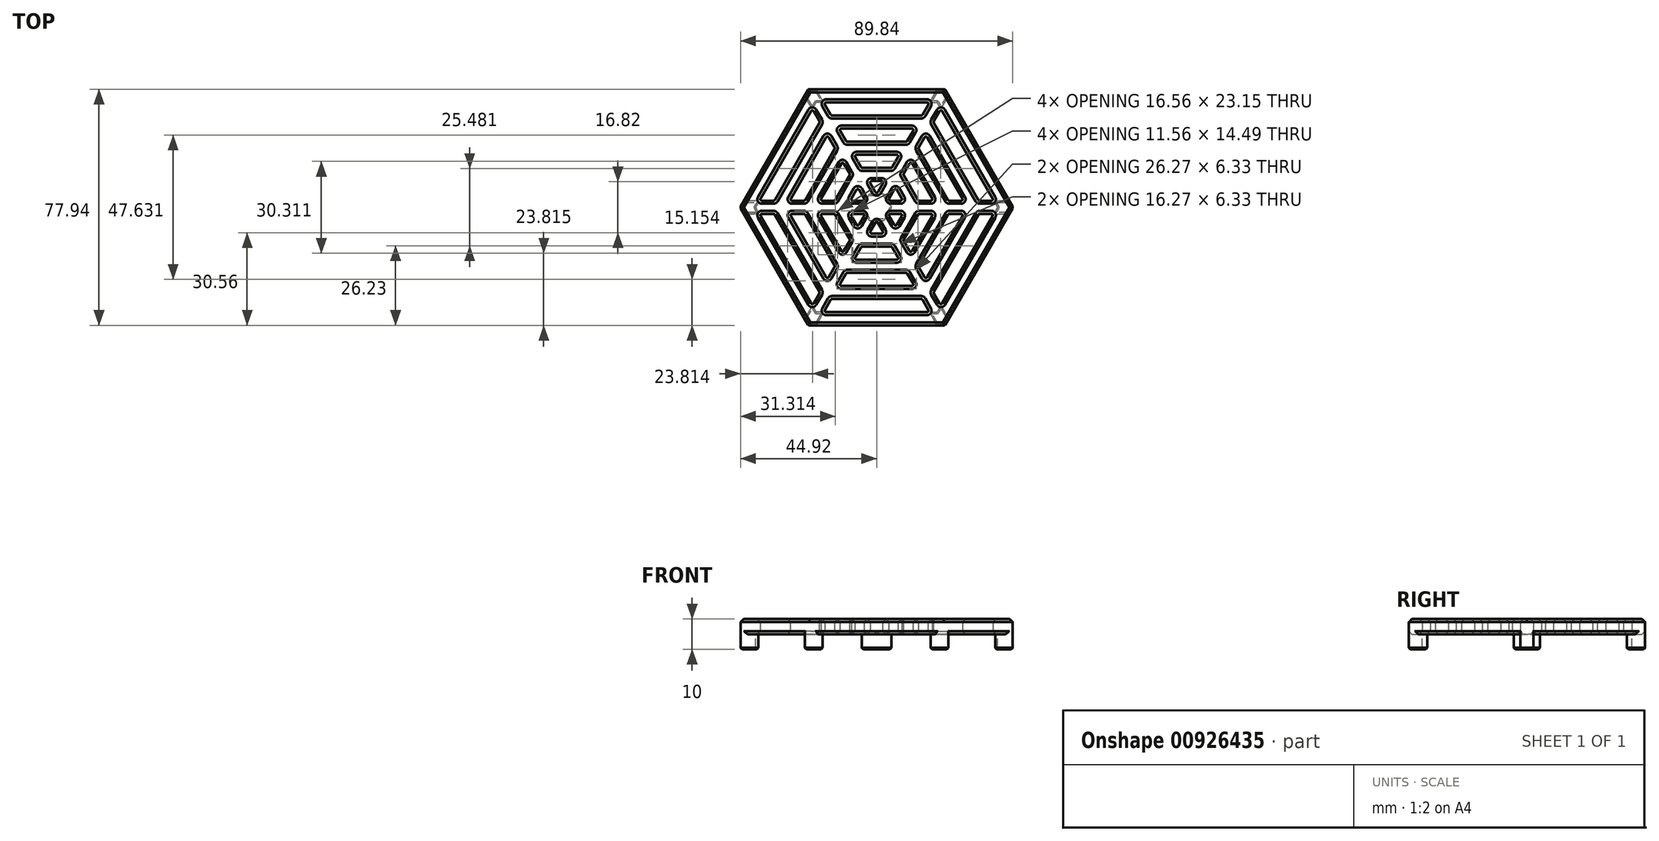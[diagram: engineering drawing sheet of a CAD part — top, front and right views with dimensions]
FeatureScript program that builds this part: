
annotation { "Feature Type Name" : "Feature", "Feature Type Description" : "" }
export const myFeature = defineFeature(function(context is Context, id is Id, definition is map)
    precondition{}
    {
        {
            var Q0;
            Q0=qCreatedBy(makeId("Top.planeOp"),FACE);
            var sketch = newSketch(context, id + "F0", { "sketchPlane" : qUnion([Q0])});
            skCircle(sketch, "E0.cCircle", {"center": v(0, 0) * mm, "radius": 45 * mm, "construction": true});
            skLineSegment(sketch, "E0.0", {"start": v(45, 0) * mm, "end": v(22.5, -38.97) * mm});
            skLineSegment(sketch, "E0.1", {"start": v(22.5, -38.97) * mm, "end": v(-22.5, -38.97) * mm});
            skLineSegment(sketch, "E0.2", {"start": v(-22.5, -38.97) * mm, "end": v(-45, 0) * mm});
            skLineSegment(sketch, "E0.3", {"start": v(-45, 0) * mm, "end": v(-22.5, 38.97) * mm});
            skLineSegment(sketch, "E0.4", {"start": v(-22.5, 38.97) * mm, "end": v(22.5, 38.97) * mm});
            skLineSegment(sketch, "E0.5", {"start": v(22.5, 38.97) * mm, "end": v(45, 0) * mm});
            skCircle(sketch, "E1.cCircle", {"center": v(0, 0) * mm, "radius": 5 * mm, "construction": true});
            skCircle(sketch, "E2.cCircle", {"center": v(0, 0) * mm, "radius": 10 * mm, "construction": true});
            skLineSegment(sketch, "E2.0", {"start": v(8.75, -2.17) * mm, "end": v(6.25, -6.5) * mm});
            skLineSegment(sketch, "E2.1", {"start": v(2.5, -8.66) * mm, "end": v(-2.5, -8.66) * mm});
            skLineSegment(sketch, "E2.2", {"start": v(-6.25, -6.5) * mm, "end": v(-8.75, -2.17) * mm});
            skLineSegment(sketch, "E2.3", {"start": v(-8.75, 2.17) * mm, "end": v(-6.25, 6.5) * mm});
            skLineSegment(sketch, "E2.4", {"start": v(-2.5, 8.66) * mm, "end": v(2.5, 8.66) * mm});
            skLineSegment(sketch, "E2.5", {"start": v(6.25, 6.5) * mm, "end": v(8.75, 2.17) * mm});
            skCircle(sketch, "E3.cCircle", {"center": v(0, 0) * mm, "radius": 15 * mm, "construction": true});
            skLineSegment(sketch, "E3.0", {"start": v(13.75, -2.17) * mm, "end": v(8.75, -10.83) * mm});
            skLineSegment(sketch, "E3.1", {"start": v(5, -13) * mm, "end": v(-5, -13) * mm});
            skLineSegment(sketch, "E3.2", {"start": v(-8.75, -10.83) * mm, "end": v(-13.75, -2.17) * mm});
            skLineSegment(sketch, "E3.3", {"start": v(-13.75, 2.17) * mm, "end": v(-8.75, 10.83) * mm});
            skLineSegment(sketch, "E3.4", {"start": v(-5, 13) * mm, "end": v(5, 13) * mm});
            skLineSegment(sketch, "E3.5", {"start": v(8.75, 10.83) * mm, "end": v(13.75, 2.17) * mm});
            skCircle(sketch, "E4.cCircle", {"center": v(0, 0) * mm, "radius": 20 * mm, "construction": true});
            skLineSegment(sketch, "E4.0", {"start": v(18.75, -2.17) * mm, "end": v(11.25, -15.16) * mm});
            skLineSegment(sketch, "E4.1", {"start": v(7.5, -17.32) * mm, "end": v(-7.5, -17.32) * mm});
            skLineSegment(sketch, "E4.2", {"start": v(-11.25, -15.16) * mm, "end": v(-18.75, -2.17) * mm});
            skLineSegment(sketch, "E4.3", {"start": v(-18.75, 2.17) * mm, "end": v(-11.25, 15.16) * mm});
            skLineSegment(sketch, "E4.4", {"start": v(-7.5, 17.32) * mm, "end": v(7.5, 17.32) * mm});
            skLineSegment(sketch, "E4.5", {"start": v(11.25, 15.16) * mm, "end": v(18.75, 2.17) * mm});
            skCircle(sketch, "E5.cCircle", {"center": v(0, 0) * mm, "radius": 25 * mm, "construction": true});
            skLineSegment(sketch, "E5.0", {"start": v(23.75, -2.17) * mm, "end": v(13.75, -19.49) * mm});
            skLineSegment(sketch, "E5.1", {"start": v(10, -21.65) * mm, "end": v(-10, -21.65) * mm});
            skLineSegment(sketch, "E5.2", {"start": v(-13.75, -19.49) * mm, "end": v(-23.75, -2.17) * mm});
            skLineSegment(sketch, "E5.3", {"start": v(-23.75, 2.17) * mm, "end": v(-13.75, 19.49) * mm});
            skLineSegment(sketch, "E5.4", {"start": v(-10, 21.65) * mm, "end": v(10, 21.65) * mm});
            skLineSegment(sketch, "E5.5", {"start": v(13.75, 19.49) * mm, "end": v(23.75, 2.17) * mm});
            skCircle(sketch, "E6.cCircle", {"center": v(0, 0) * mm, "radius": 30 * mm, "construction": true});
            skLineSegment(sketch, "E6.0", {"start": v(28.75, -2.17) * mm, "end": v(16.25, -23.82) * mm});
            skLineSegment(sketch, "E6.1", {"start": v(12.5, -25.98) * mm, "end": v(-12.5, -25.98) * mm});
            skLineSegment(sketch, "E6.2", {"start": v(-16.25, -23.82) * mm, "end": v(-28.75, -2.17) * mm});
            skLineSegment(sketch, "E6.3", {"start": v(-28.75, 2.17) * mm, "end": v(-16.25, 23.82) * mm});
            skLineSegment(sketch, "E6.4", {"start": v(-12.5, 25.98) * mm, "end": v(12.5, 25.98) * mm});
            skLineSegment(sketch, "E6.5", {"start": v(16.25, 23.82) * mm, "end": v(28.75, 2.17) * mm});
            skCircle(sketch, "E7.cCircle", {"center": v(0, 0) * mm, "radius": 35 * mm, "construction": true});
            skLineSegment(sketch, "E7.0", {"start": v(33.75, -2.17) * mm, "end": v(18.75, -28.15) * mm});
            skLineSegment(sketch, "E7.1", {"start": v(15, -30.31) * mm, "end": v(-15, -30.31) * mm});
            skLineSegment(sketch, "E7.2", {"start": v(-18.75, -28.15) * mm, "end": v(-33.75, -2.17) * mm});
            skLineSegment(sketch, "E7.3", {"start": v(-33.75, 2.17) * mm, "end": v(-18.75, 28.15) * mm});
            skLineSegment(sketch, "E7.4", {"start": v(-15, 30.31) * mm, "end": v(15, 30.31) * mm});
            skLineSegment(sketch, "E7.5", {"start": v(18.75, 28.15) * mm, "end": v(33.75, 2.17) * mm});
            skCircle(sketch, "E8.cCircle", {"center": v(0, 0) * mm, "radius": 40 * mm, "construction": true});
            skLineSegment(sketch, "E8.1", {"start": v(17.5, -34.64) * mm, "end": v(-17.5, -34.64) * mm});
            skLineSegment(sketch, "E8.2", {"start": v(-21.25, -32.48) * mm, "end": v(-38.75, -2.17) * mm});
            skLineSegment(sketch, "E8.3", {"start": v(-38.75, 2.17) * mm, "end": v(-21.25, 32.48) * mm});
            skLineSegment(sketch, "E8.4", {"start": v(-17.5, 34.64) * mm, "end": v(17.5, 34.64) * mm});
            skLineSegment(sketch, "E8.5", {"start": v(21.25, 32.48) * mm, "end": v(38.75, 2.17) * mm});
            skLineSegment(sketch, "E9", {"start": v(0, -4.33) * mm, "end": v(2.5, -8.66) * mm});
            skLineSegment(sketch, "E10", {"start": v(0, -4.33) * mm, "end": v(-2.5, -8.66) * mm});
            skLineSegment(sketch, "E11", {"start": v(3.75, -2.17) * mm, "end": v(6.25, -6.5) * mm});
            skLineSegment(sketch, "E12", {"start": v(38.75, -2.17) * mm, "end": v(33.75, -2.17) * mm});
            skLineSegment(sketch, "E13", {"start": v(3.75, 2.17) * mm, "end": v(8.75, 2.17) * mm});
            skLineSegment(sketch, "E14", {"start": v(3.75, 2.17) * mm, "end": v(6.25, 6.5) * mm});
            skLineSegment(sketch, "E15", {"start": v(0, 4.33) * mm, "end": v(2.5, 8.66) * mm});
            skLineSegment(sketch, "E16", {"start": v(0, 4.33) * mm, "end": v(-2.5, 8.66) * mm});
            skLineSegment(sketch, "E17", {"start": v(-3.75, 2.17) * mm, "end": v(-6.25, 6.5) * mm});
            skLineSegment(sketch, "E18", {"start": v(-3.75, 2.17) * mm, "end": v(-8.75, 2.17) * mm});
            skLineSegment(sketch, "E19", {"start": v(-3.75, -2.17) * mm, "end": v(-8.75, -2.17) * mm});
            skLineSegment(sketch, "E20", {"start": v(-3.75, -2.17) * mm, "end": v(-6.25, -6.5) * mm});
            skPoint(sketch, "E21.orphan", {"position": v(5, 8.66) * mm});
            skPoint(sketch, "E22.orphan", {"position": v(7.5, 13) * mm});
            skPoint(sketch, "E23.orphan", {"position": v(10, 17.32) * mm});
            skPoint(sketch, "E24.orphan", {"position": v(12.5, 21.65) * mm});
            skPoint(sketch, "E25.orphan", {"position": v(15, 25.98) * mm});
            skPoint(sketch, "E26.orphan", {"position": v(17.5, 30.31) * mm});
            skPoint(sketch, "E27.orphan", {"position": v(20, 34.64) * mm});
            skPoint(sketch, "E28.orphan", {"position": v(2.5, 4.33) * mm});
            skPoint(sketch, "E29.orphan", {"position": v(43.75, -2.17) * mm});
            skLineSegment(sketch, "E30.trimOffspring", {"start": v(-15, 30.31) * mm, "end": v(-17.5, 34.64) * mm});
            skLineSegment(sketch, "E31.trimOffspring", {"start": v(-18.75, 28.15) * mm, "end": v(-21.25, 32.48) * mm});
            skLineSegment(sketch, "E32.trimOffspring", {"start": v(15, 30.31) * mm, "end": v(17.5, 34.64) * mm});
            skLineSegment(sketch, "E33.trimOffspring", {"start": v(18.75, 28.15) * mm, "end": v(21.25, 32.48) * mm});
            skLineSegment(sketch, "E34.trimOffspring", {"start": v(33.75, 2.17) * mm, "end": v(38.75, 2.17) * mm});
            skLineSegment(sketch, "E35.trimOffspring", {"start": v(28.75, -2.17) * mm, "end": v(23.75, -2.17) * mm});
            skLineSegment(sketch, "E36.trimOffspring", {"start": v(18.75, -28.15) * mm, "end": v(21.25, -32.48) * mm});
            skLineSegment(sketch, "E37.trimOffspring", {"start": v(15, -30.31) * mm, "end": v(17.5, -34.64) * mm});
            skLineSegment(sketch, "E38.trimOffspring", {"start": v(-15, -30.31) * mm, "end": v(-17.5, -34.64) * mm});
            skLineSegment(sketch, "E39.trimOffspring", {"start": v(-18.75, -28.15) * mm, "end": v(-21.25, -32.48) * mm});
            skLineSegment(sketch, "E40.trimOffspring", {"start": v(-33.75, -2.17) * mm, "end": v(-38.75, -2.17) * mm});
            skLineSegment(sketch, "E41.trimOffspring", {"start": v(-33.75, 2.17) * mm, "end": v(-38.75, 2.17) * mm});
            skLineSegment(sketch, "E42.trimOffspring", {"start": v(-13.75, 19.49) * mm, "end": v(-16.25, 23.82) * mm});
            skLineSegment(sketch, "E43.trimOffspring", {"start": v(-10, 21.65) * mm, "end": v(-12.5, 25.98) * mm});
            skLineSegment(sketch, "E44.trimOffspring", {"start": v(10, 21.65) * mm, "end": v(12.5, 25.98) * mm});
            skLineSegment(sketch, "E45.trimOffspring", {"start": v(13.75, 19.49) * mm, "end": v(16.25, 23.82) * mm});
            skLineSegment(sketch, "E46.trimOffspring", {"start": v(23.75, 2.17) * mm, "end": v(28.75, 2.17) * mm});
            skLineSegment(sketch, "E47.trimOffspring", {"start": v(18.75, -2.17) * mm, "end": v(13.75, -2.17) * mm});
            skLineSegment(sketch, "E48.trimOffspring", {"start": v(13.75, -19.49) * mm, "end": v(16.25, -23.82) * mm});
            skLineSegment(sketch, "E49.trimOffspring", {"start": v(10, -21.65) * mm, "end": v(12.5, -25.98) * mm});
            skLineSegment(sketch, "E50.trimOffspring", {"start": v(-10, -21.65) * mm, "end": v(-12.5, -25.98) * mm});
            skLineSegment(sketch, "E51.trimOffspring", {"start": v(-13.75, -19.49) * mm, "end": v(-16.25, -23.82) * mm});
            skLineSegment(sketch, "E52.trimOffspring", {"start": v(-23.75, -2.17) * mm, "end": v(-28.75, -2.17) * mm});
            skLineSegment(sketch, "E53.trimOffspring", {"start": v(-23.75, 2.17) * mm, "end": v(-28.75, 2.17) * mm});
            skLineSegment(sketch, "E54.trimOffspring", {"start": v(-8.75, 10.83) * mm, "end": v(-11.25, 15.16) * mm});
            skLineSegment(sketch, "E55.trimOffspring", {"start": v(-5, 13) * mm, "end": v(-7.5, 17.32) * mm});
            skLineSegment(sketch, "E56.trimOffspring", {"start": v(5, 13) * mm, "end": v(7.5, 17.32) * mm});
            skLineSegment(sketch, "E57.trimOffspring", {"start": v(8.75, 10.83) * mm, "end": v(11.25, 15.16) * mm});
            skLineSegment(sketch, "E58.trimOffspring", {"start": v(13.75, 2.17) * mm, "end": v(18.75, 2.17) * mm});
            skLineSegment(sketch, "E59.trimOffspring", {"start": v(8.75, -2.17) * mm, "end": v(3.75, -2.17) * mm});
            skLineSegment(sketch, "E60.trimOffspring", {"start": v(8.75, -10.83) * mm, "end": v(11.25, -15.16) * mm});
            skLineSegment(sketch, "E61.trimOffspring", {"start": v(5, -13) * mm, "end": v(7.5, -17.32) * mm});
            skLineSegment(sketch, "E62.trimOffspring", {"start": v(-5, -13) * mm, "end": v(-7.5, -17.32) * mm});
            skLineSegment(sketch, "E63.trimOffspring", {"start": v(-8.75, -10.83) * mm, "end": v(-11.25, -15.16) * mm});
            skLineSegment(sketch, "E64.trimOffspring", {"start": v(-13.75, -2.17) * mm, "end": v(-18.75, -2.17) * mm});
            skLineSegment(sketch, "E65.trimOffspring", {"start": v(-13.75, 2.17) * mm, "end": v(-18.75, 2.17) * mm});
            skPoint(sketch, "E66.orphan", {"position": v(10, 0) * mm});
            skPoint(sketch, "E67.orphan", {"position": v(15, 0) * mm});
            skPoint(sketch, "E68.orphan", {"position": v(20, 0) * mm});
            skPoint(sketch, "E69.orphan", {"position": v(25, 0) * mm});
            skPoint(sketch, "E70.orphan", {"position": v(30, 0) * mm});
            skPoint(sketch, "E71.orphan", {"position": v(35, 0) * mm});
            skPoint(sketch, "E72.orphan", {"position": v(40, 0) * mm});
            skPoint(sketch, "E73.orphan", {"position": v(5, -8.66) * mm});
            skPoint(sketch, "E74.orphan", {"position": v(7.5, -13) * mm});
            skPoint(sketch, "E75.orphan", {"position": v(10, -17.32) * mm});
            skPoint(sketch, "E76.orphan", {"position": v(12.5, -21.65) * mm});
            skPoint(sketch, "E77.orphan", {"position": v(15, -25.98) * mm});
            skPoint(sketch, "E78.orphan", {"position": v(17.5, -30.31) * mm});
            skPoint(sketch, "E79.orphan", {"position": v(20, -34.64) * mm});
            skLineSegment(sketch, "E80", {"start": v(38.75, -2.17) * mm, "end": v(21.25, -32.48) * mm});
            skPoint(sketch, "E81.orphan", {"position": v(-5, -8.66) * mm});
            skPoint(sketch, "E82.orphan", {"position": v(-7.5, -13) * mm});
            skPoint(sketch, "E83.orphan", {"position": v(-10, -17.32) * mm});
            skPoint(sketch, "E84.orphan", {"position": v(-12.5, -21.65) * mm});
            skPoint(sketch, "E85.orphan", {"position": v(-15, -25.98) * mm});
            skPoint(sketch, "E86.orphan", {"position": v(-17.5, -30.31) * mm});
            skPoint(sketch, "E87.orphan", {"position": v(-20, -34.64) * mm});
            skPoint(sketch, "E88.orphan", {"position": v(-10, 0) * mm});
            skPoint(sketch, "E89.orphan", {"position": v(-15, 0) * mm});
            skPoint(sketch, "E90.orphan", {"position": v(-20, 0) * mm});
            skPoint(sketch, "E91.orphan", {"position": v(-25, 0) * mm});
            skPoint(sketch, "E92.orphan", {"position": v(-30, 0) * mm});
            skPoint(sketch, "E93.orphan", {"position": v(-35, 0) * mm});
            skPoint(sketch, "E94.orphan", {"position": v(-40, 0) * mm});
            skPoint(sketch, "E95.orphan", {"position": v(-5, 8.66) * mm});
            skPoint(sketch, "E96.orphan", {"position": v(-7.5, 13) * mm});
            skPoint(sketch, "E97.orphan", {"position": v(-10, 17.32) * mm});
            skPoint(sketch, "E98.orphan", {"position": v(-12.5, 21.65) * mm});
            skPoint(sketch, "E99.orphan", {"position": v(-15, 25.98) * mm});
            skPoint(sketch, "E100.orphan", {"position": v(-17.5, 30.31) * mm});
            skPoint(sketch, "E101.orphan", {"position": v(-20, 34.64) * mm});
            skSolve(sketch);
        }
        {
            var Q0;
            Q0=makeQuery(id+"F0.imprint","IMPRINT",FACE,{"disambiguationData":[TD([[makeQuery(id+"F0.imprint","IMPRINT",EDGE,{"derivedFrom":sQuery(id+"F0.wireOp",EDGE,"E0.0")}),-1.0]])]});
            extrude(context, id + "F1", {"entities" : qUnion([Q0]), "depth" : 5 * mm, "offsetDistance" : 25 * mm});
        }
        {
            var Q0;
            Q0=makeQuery(id+"F1.opExtrude","CAP_FACE",FACE,{"disambiguationData":[OSD([sQuery(id+"F0.wireOp",EDGE,"E0.0"),sQuery(id+"F0.wireOp",EDGE,"E0.1"),sQuery(id+"F0.wireOp",EDGE,"E0.2"),sQuery(id+"F0.wireOp",EDGE,"E0.3"),sQuery(id+"F0.wireOp",EDGE,"E0.4"),sQuery(id+"F0.wireOp",EDGE,"E0.5"),sQuery(id+"F0.wireOp",EDGE,"E2.0"),sQuery(id+"F0.wireOp",EDGE,"E2.1"),sQuery(id+"F0.wireOp",EDGE,"E2.2"),sQuery(id+"F0.wireOp",EDGE,"E2.3"),sQuery(id+"F0.wireOp",EDGE,"E2.4"),sQuery(id+"F0.wireOp",EDGE,"E2.5"),sQuery(id+"F0.wireOp",EDGE,"E3.0"),sQuery(id+"F0.wireOp",EDGE,"E3.1"),sQuery(id+"F0.wireOp",EDGE,"E3.2"),sQuery(id+"F0.wireOp",EDGE,"E3.3"),sQuery(id+"F0.wireOp",EDGE,"E3.4"),sQuery(id+"F0.wireOp",EDGE,"E3.5"),sQuery(id+"F0.wireOp",EDGE,"E4.0"),sQuery(id+"F0.wireOp",EDGE,"E4.1"),sQuery(id+"F0.wireOp",EDGE,"E4.2"),sQuery(id+"F0.wireOp",EDGE,"E4.3"),sQuery(id+"F0.wireOp",EDGE,"E4.4"),sQuery(id+"F0.wireOp",EDGE,"E4.5"),sQuery(id+"F0.wireOp",EDGE,"E5.0"),sQuery(id+"F0.wireOp",EDGE,"E5.1"),sQuery(id+"F0.wireOp",EDGE,"E5.2"),sQuery(id+"F0.wireOp",EDGE,"E5.3"),sQuery(id+"F0.wireOp",EDGE,"E5.4"),sQuery(id+"F0.wireOp",EDGE,"E5.5"),sQuery(id+"F0.wireOp",EDGE,"E6.0"),sQuery(id+"F0.wireOp",EDGE,"E6.1"),sQuery(id+"F0.wireOp",EDGE,"E6.2"),sQuery(id+"F0.wireOp",EDGE,"E6.3"),sQuery(id+"F0.wireOp",EDGE,"E6.4"),sQuery(id+"F0.wireOp",EDGE,"E6.5"),sQuery(id+"F0.wireOp",EDGE,"E7.0"),sQuery(id+"F0.wireOp",EDGE,"E7.1"),sQuery(id+"F0.wireOp",EDGE,"E7.2"),sQuery(id+"F0.wireOp",EDGE,"E7.3"),sQuery(id+"F0.wireOp",EDGE,"E7.4"),sQuery(id+"F0.wireOp",EDGE,"E7.5"),sQuery(id+"F0.wireOp",EDGE,"E8.1"),sQuery(id+"F0.wireOp",EDGE,"E8.2"),sQuery(id+"F0.wireOp",EDGE,"E8.3"),sQuery(id+"F0.wireOp",EDGE,"E8.4"),sQuery(id+"F0.wireOp",EDGE,"E8.5"),sQuery(id+"F0.wireOp",EDGE,"E9"),sQuery(id+"F0.wireOp",EDGE,"E10"),sQuery(id+"F0.wireOp",EDGE,"E11"),sQuery(id+"F0.wireOp",EDGE,"E12"),sQuery(id+"F0.wireOp",EDGE,"E13"),sQuery(id+"F0.wireOp",EDGE,"E14"),sQuery(id+"F0.wireOp",EDGE,"E15"),sQuery(id+"F0.wireOp",EDGE,"E16"),sQuery(id+"F0.wireOp",EDGE,"E17"),sQuery(id+"F0.wireOp",EDGE,"E18"),sQuery(id+"F0.wireOp",EDGE,"E19"),sQuery(id+"F0.wireOp",EDGE,"E20"),sQuery(id+"F0.wireOp",EDGE,"E30.trimOffspring"),sQuery(id+"F0.wireOp",EDGE,"E31.trimOffspring"),sQuery(id+"F0.wireOp",EDGE,"E32.trimOffspring"),sQuery(id+"F0.wireOp",EDGE,"E33.trimOffspring"),sQuery(id+"F0.wireOp",EDGE,"E34.trimOffspring"),sQuery(id+"F0.wireOp",EDGE,"E35.trimOffspring"),sQuery(id+"F0.wireOp",EDGE,"E36.trimOffspring"),sQuery(id+"F0.wireOp",EDGE,"E37.trimOffspring"),sQuery(id+"F0.wireOp",EDGE,"E38.trimOffspring"),sQuery(id+"F0.wireOp",EDGE,"E39.trimOffspring"),sQuery(id+"F0.wireOp",EDGE,"E40.trimOffspring"),sQuery(id+"F0.wireOp",EDGE,"E41.trimOffspring"),sQuery(id+"F0.wireOp",EDGE,"E42.trimOffspring"),sQuery(id+"F0.wireOp",EDGE,"E43.trimOffspring"),sQuery(id+"F0.wireOp",EDGE,"E44.trimOffspring"),sQuery(id+"F0.wireOp",EDGE,"E45.trimOffspring"),sQuery(id+"F0.wireOp",EDGE,"E46.trimOffspring"),sQuery(id+"F0.wireOp",EDGE,"E47.trimOffspring"),sQuery(id+"F0.wireOp",EDGE,"E48.trimOffspring"),sQuery(id+"F0.wireOp",EDGE,"E49.trimOffspring"),sQuery(id+"F0.wireOp",EDGE,"E50.trimOffspring"),sQuery(id+"F0.wireOp",EDGE,"E51.trimOffspring"),sQuery(id+"F0.wireOp",EDGE,"E52.trimOffspring"),sQuery(id+"F0.wireOp",EDGE,"E53.trimOffspring"),sQuery(id+"F0.wireOp",EDGE,"E54.trimOffspring"),sQuery(id+"F0.wireOp",EDGE,"E55.trimOffspring"),sQuery(id+"F0.wireOp",EDGE,"E56.trimOffspring"),sQuery(id+"F0.wireOp",EDGE,"E57.trimOffspring"),sQuery(id+"F0.wireOp",EDGE,"E58.trimOffspring"),sQuery(id+"F0.wireOp",EDGE,"E59.trimOffspring"),sQuery(id+"F0.wireOp",EDGE,"E60.trimOffspring"),sQuery(id+"F0.wireOp",EDGE,"E61.trimOffspring"),sQuery(id+"F0.wireOp",EDGE,"E62.trimOffspring"),sQuery(id+"F0.wireOp",EDGE,"E63.trimOffspring"),sQuery(id+"F0.wireOp",EDGE,"E64.trimOffspring"),sQuery(id+"F0.wireOp",EDGE,"E65.trimOffspring"),sQuery(id+"F0.wireOp",EDGE,"E80")])],"isStart":true});
            var sketch = newSketch(context, id + "F2", { "sketchPlane" : qUnion([Q0])});
            skLineSegment(sketch, "E102", {"start": v(21.25, 32.48) * mm, "end": v(23.75, 36.8) * mm});
            skLineSegment(sketch, "E103", {"start": v(20, 38.97) * mm, "end": v(17.5, 34.64) * mm});
            skLineSegment(sketch, "E104", {"start": v(21.25, 32.48) * mm, "end": v(20, 34.64) * mm});
            skLineSegment(sketch, "E105", {"start": v(17.5, 34.64) * mm, "end": v(20, 34.64) * mm});
            skLineSegment(sketch, "E106", {"start": v(-17.5, 34.64) * mm, "end": v(-20, 38.97) * mm});
            skLineSegment(sketch, "E107", {"start": v(-21.25, 32.48) * mm, "end": v(-23.75, 36.8) * mm});
            skLineSegment(sketch, "E108", {"start": v(-17.5, 34.64) * mm, "end": v(-20, 34.64) * mm});
            skLineSegment(sketch, "E109", {"start": v(-21.25, 32.48) * mm, "end": v(-20, 34.64) * mm});
            skLineSegment(sketch, "E110", {"start": v(-38.75, 2.17) * mm, "end": v(-43.75, 2.17) * mm});
            skLineSegment(sketch, "E111", {"start": v(-38.75, -2.17) * mm, "end": v(-43.75, -2.17) * mm});
            skLineSegment(sketch, "E112", {"start": v(-38.75, 2.17) * mm, "end": v(-40, 0) * mm});
            skLineSegment(sketch, "E113", {"start": v(-38.75, -2.17) * mm, "end": v(-40, 0) * mm});
            skLineSegment(sketch, "E114", {"start": v(-21.25, -32.48) * mm, "end": v(-23.75, -36.8) * mm});
            skLineSegment(sketch, "E115", {"start": v(-17.5, -34.64) * mm, "end": v(-20, -38.97) * mm});
            skLineSegment(sketch, "E116", {"start": v(-21.25, -32.48) * mm, "end": v(-20, -34.64) * mm});
            skLineSegment(sketch, "E117", {"start": v(-17.5, -34.64) * mm, "end": v(-20, -34.64) * mm});
            skLineSegment(sketch, "E118", {"start": v(21.25, -32.48) * mm, "end": v(23.75, -36.8) * mm});
            skLineSegment(sketch, "E119", {"start": v(17.5, -34.64) * mm, "end": v(20, -38.97) * mm});
            skLineSegment(sketch, "E120", {"start": v(17.5, -34.64) * mm, "end": v(20, -34.64) * mm});
            skLineSegment(sketch, "E121", {"start": v(21.25, -32.48) * mm, "end": v(20, -34.64) * mm});
            skLineSegment(sketch, "E122", {"start": v(38.75, 2.17) * mm, "end": v(40, 0) * mm});
            skLineSegment(sketch, "E123", {"start": v(38.75, -2.17) * mm, "end": v(40, 0) * mm});
            skLineSegment(sketch, "E124", {"start": v(38.75, 2.17) * mm, "end": v(43.75, 2.17) * mm});
            skLineSegment(sketch, "E125", {"start": v(38.75, -2.17) * mm, "end": v(43.75, -2.17) * mm});
            skCircle(sketch, "E126.cCircle", {"center": v(0, 0) * mm, "radius": 4.33 * mm, "construction": true});
            skLineSegment(sketch, "E126.0", {"start": v(5, 0) * mm, "end": v(2.5, -4.33) * mm});
            skLineSegment(sketch, "E126.1", {"start": v(2.5, -4.33) * mm, "end": v(-2.5, -4.33) * mm});
            skLineSegment(sketch, "E126.2", {"start": v(-2.5, -4.33) * mm, "end": v(-5, 0) * mm});
            skLineSegment(sketch, "E126.3", {"start": v(-5, 0) * mm, "end": v(-2.5, 4.33) * mm});
            skLineSegment(sketch, "E126.4", {"start": v(-2.5, 4.33) * mm, "end": v(2.5, 4.33) * mm});
            skLineSegment(sketch, "E126.5", {"start": v(2.5, 4.33) * mm, "end": v(5, 0) * mm});
            skPoint(sketch, "E126.0.midPoint", {"position": v(3.75, -2.17) * mm});
            skSolve(sketch);
        }
        {
            var Q0;
            {var subQ1=sQuery(id+"F2.wireOp",EDGE,"E106");Q0=makeQuery(id+"F2.imprint","IMPRINT",FACE,{"disambiguationData":[TD([[makeQuery(id+"F2.imprint","IMPRINT",EDGE,{"derivedFrom":subQ1}),1.0]])]});}
            var Q1;
            {var subQ1=sQuery(id+"F2.wireOp",EDGE,"E102");Q1=makeQuery(id+"F2.imprint","IMPRINT",FACE,{"disambiguationData":[TD([[makeQuery(id+"F2.imprint","IMPRINT",EDGE,{"derivedFrom":subQ1}),1.0]])]});}
            var Q2;
            Q2=makeQuery(id+"F2.imprint","IMPRINT",FACE,{"disambiguationData":[TD([[makeQuery(id+"F2.imprint","IMPRINT",EDGE,{"derivedFrom":sQuery(id+"F2.wireOp",EDGE,"E122")}),1.0]])]});
            var Q3;
            {var subQ2=sQuery(id+"F2.wireOp",EDGE,"E126.5");var subQ12=sQuery(id+"F2.wireOp",EDGE,"E126.0");var subQ14=makeQuery(id+"F2.imprint","INTERSECT",VERTEX,{"derivedFrom":[subQ12,subQ2]});Q3=makeQuery(id+"F2.imprint","IMPRINT",FACE,{"disambiguationData":[TD([[makeQuery(id+"F2.imprint","IMPRINT",EDGE,{"disambiguationData":[TD([[subQ14,-1.0]])],"derivedFrom":subQ12}),-1.0]])]});}
            var Q4;
            {var subQ1=sQuery(id+"F2.wireOp",EDGE,"E110");Q4=makeQuery(id+"F2.imprint","IMPRINT",FACE,{"disambiguationData":[TD([[makeQuery(id+"F2.imprint","IMPRINT",EDGE,{"derivedFrom":subQ1}),1.0]])]});}
            var Q5;
            {var subQ3=sQuery(id+"F2.wireOp",EDGE,"E114");Q5=makeQuery(id+"F2.imprint","IMPRINT",FACE,{"disambiguationData":[TD([[makeQuery(id+"F2.imprint","IMPRINT",EDGE,{"derivedFrom":subQ3}),1.0]])]});}
            var Q6;
            {var subQ4=sQuery(id+"F2.wireOp",EDGE,"E118");Q6=makeQuery(id+"F2.imprint","IMPRINT",FACE,{"disambiguationData":[TD([[makeQuery(id+"F2.imprint","IMPRINT",EDGE,{"derivedFrom":subQ4}),-1.0]])]});}
            extrude(context, id + "F3", {"entities" : qUnion([Q0, Q1, Q2, Q3, Q4, Q5, Q6]), "operationType" : NewBodyOperationType.ADD, "depth" : 5 * mm, "offsetDistance" : 25 * mm});
        }
        {
            var Q0;
            Q0=makeQuery(id+"F1.opExtrude","SWEPT_EDGE",EDGE,{"disambiguationData":[OSD([sQuery(id+"F0.wireOp",EDGE,"E36.trimOffspring"),sQuery(id+"F0.wireOp",EDGE,"E80")])]});
            var Q1;
            Q1=makeQuery(id+"F1.opExtrude","SWEPT_EDGE",EDGE,{"disambiguationData":[OSD([sQuery(id+"F0.wireOp",EDGE,"E7.2"),sQuery(id+"F0.wireOp",EDGE,"E40.trimOffspring")])]});
            var Q2;
            Q2=makeQuery(id+"F1.opExtrude","SWEPT_EDGE",EDGE,{"disambiguationData":[OSD([sQuery(id+"F0.wireOp",EDGE,"E11"),sQuery(id+"F0.wireOp",EDGE,"E59.trimOffspring")])]});
            var Q3;
            Q3=makeQuery(id+"F3.opExtrude","SWEPT_EDGE",EDGE,{"disambiguationData":[OSD([sQuery(id+"F2.wireOp",EDGE,"E126.0"),sQuery(id+"F2.wireOp",EDGE,"E126.1")])]});
            var Q4;
            Q4=makeQuery(id+"F3.opExtrude","SWEPT_EDGE",EDGE,{"disambiguationData":[OSD([sQuery(id+"F2.wireOp",EDGE,"E126.1"),sQuery(id+"F2.wireOp",EDGE,"E126.2")])]});
            var Q5;
            Q5=makeQuery(id+"F3.opExtrude","SWEPT_EDGE",EDGE,{"disambiguationData":[OSD([sQuery(id+"F2.wireOp",EDGE,"E126.0"),sQuery(id+"F2.wireOp",EDGE,"E126.5")])]});
            var Q6;
            Q6=makeQuery(id+"F3.opExtrude","SWEPT_EDGE",EDGE,{"disambiguationData":[OSD([sQuery(id+"F2.wireOp",EDGE,"E126.4"),sQuery(id+"F2.wireOp",EDGE,"E126.5")])]});
            var Q7;
            Q7=makeQuery(id+"F3.opExtrude","SWEPT_EDGE",EDGE,{"disambiguationData":[OSD([sQuery(id+"F2.wireOp",EDGE,"E126.3"),sQuery(id+"F2.wireOp",EDGE,"E126.4")])]});
            var Q8;
            Q8=makeQuery(id+"F3.opExtrude","SWEPT_EDGE",EDGE,{"disambiguationData":[OSD([sQuery(id+"F2.wireOp",EDGE,"E126.2"),sQuery(id+"F2.wireOp",EDGE,"E126.3")])]});
            var Q9;
            Q9=makeQuery(id+"F3.opExtrude","SWEPT_EDGE",EDGE,{"disambiguationData":[OSD([sQuery(id+"F0.wireOp",EDGE,"E8.1"),sQuery(id+"F0.wireOp",EDGE,"E37.trimOffspring"),sQuery(id+"F2.wireOp",EDGE,"E103"),sQuery(id+"F2.wireOp",EDGE,"E105")])]});
            var Q10;
            Q10=makeQuery(id+"F3.opExtrude","SWEPT_EDGE",EDGE,{"disambiguationData":[OSD([sQuery(id+"F2.wireOp",EDGE,"E104"),sQuery(id+"F2.wireOp",EDGE,"E105")])]});
            var Q11;
            Q11=makeQuery(id+"F3.opExtrude","SWEPT_EDGE",EDGE,{"disambiguationData":[OSD([sQuery(id+"F0.wireOp",EDGE,"E0.0"),sQuery(id+"F2.wireOp",EDGE,"E124")])]});
            var Q12;
            Q12=makeQuery(id+"F3.opExtrude","SWEPT_EDGE",EDGE,{"disambiguationData":[OSD([sQuery(id+"F0.wireOp",EDGE,"E0.5"),sQuery(id+"F2.wireOp",EDGE,"E125")])]});
            var Q13;
            Q13=makeQuery(id+"F3.opExtrude","SWEPT_EDGE",EDGE,{"disambiguationData":[OSD([sQuery(id+"F0.wireOp",EDGE,"E8.5"),sQuery(id+"F0.wireOp",EDGE,"E34.trimOffspring"),sQuery(id+"F2.wireOp",EDGE,"E123"),sQuery(id+"F2.wireOp",EDGE,"E125")])]});
            var Q14;
            Q14=makeQuery(id+"F3.opExtrude","SWEPT_EDGE",EDGE,{"disambiguationData":[OSD([sQuery(id+"F2.wireOp",EDGE,"E122"),sQuery(id+"F2.wireOp",EDGE,"E123")])]});
            var Q15;
            Q15=makeQuery(id+"F3.opExtrude","SWEPT_EDGE",EDGE,{"disambiguationData":[OSD([sQuery(id+"F0.wireOp",EDGE,"E12"),sQuery(id+"F0.wireOp",EDGE,"E80"),sQuery(id+"F2.wireOp",EDGE,"E122"),sQuery(id+"F2.wireOp",EDGE,"E124")])]});
            var Q16;
            Q16=makeQuery(id+"F3.opExtrude","SWEPT_EDGE",EDGE,{"disambiguationData":[OSD([sQuery(id+"F0.wireOp",EDGE,"E0.2"),sQuery(id+"F2.wireOp",EDGE,"E107")])]});
            var Q17;
            Q17=makeQuery(id+"F3.opExtrude","SWEPT_EDGE",EDGE,{"disambiguationData":[OSD([sQuery(id+"F0.wireOp",EDGE,"E0.1"),sQuery(id+"F2.wireOp",EDGE,"E106")])]});
            var Q18;
            Q18=makeQuery(id+"F3.opExtrude","SWEPT_EDGE",EDGE,{"disambiguationData":[OSD([sQuery(id+"F2.wireOp",EDGE,"E108"),sQuery(id+"F2.wireOp",EDGE,"E109")])]});
            var Q19;
            Q19=makeQuery(id+"F3.opExtrude","SWEPT_EDGE",EDGE,{"disambiguationData":[OSD([sQuery(id+"F0.wireOp",EDGE,"E8.2"),sQuery(id+"F0.wireOp",EDGE,"E39.trimOffspring"),sQuery(id+"F2.wireOp",EDGE,"E107"),sQuery(id+"F2.wireOp",EDGE,"E109")])]});
            var Q20;
            Q20=makeQuery(id+"F3.opExtrude","SWEPT_EDGE",EDGE,{"disambiguationData":[OSD([sQuery(id+"F0.wireOp",EDGE,"E8.1"),sQuery(id+"F0.wireOp",EDGE,"E38.trimOffspring"),sQuery(id+"F2.wireOp",EDGE,"E106"),sQuery(id+"F2.wireOp",EDGE,"E108")])]});
            var Q21;
            Q21=makeQuery(id+"F3.opExtrude","SWEPT_EDGE",EDGE,{"disambiguationData":[OSD([sQuery(id+"F0.wireOp",EDGE,"E0.2"),sQuery(id+"F2.wireOp",EDGE,"E110")])]});
            var Q22;
            Q22=makeQuery(id+"F3.opExtrude","SWEPT_EDGE",EDGE,{"disambiguationData":[OSD([sQuery(id+"F0.wireOp",EDGE,"E8.2"),sQuery(id+"F0.wireOp",EDGE,"E40.trimOffspring"),sQuery(id+"F2.wireOp",EDGE,"E110"),sQuery(id+"F2.wireOp",EDGE,"E112")])]});
            var Q23;
            Q23=makeQuery(id+"F3.opExtrude","SWEPT_EDGE",EDGE,{"disambiguationData":[OSD([sQuery(id+"F0.wireOp",EDGE,"E0.3"),sQuery(id+"F2.wireOp",EDGE,"E111")])]});
            var Q24;
            Q24=makeQuery(id+"F3.opExtrude","SWEPT_EDGE",EDGE,{"disambiguationData":[OSD([sQuery(id+"F0.wireOp",EDGE,"E8.3"),sQuery(id+"F0.wireOp",EDGE,"E41.trimOffspring"),sQuery(id+"F2.wireOp",EDGE,"E111"),sQuery(id+"F2.wireOp",EDGE,"E113")])]});
            var Q25;
            Q25=makeQuery(id+"F3.opExtrude","SWEPT_EDGE",EDGE,{"disambiguationData":[OSD([sQuery(id+"F2.wireOp",EDGE,"E112"),sQuery(id+"F2.wireOp",EDGE,"E113")])]});
            var Q26;
            Q26=makeQuery(id+"F3.opExtrude","SWEPT_EDGE",EDGE,{"disambiguationData":[OSD([sQuery(id+"F0.wireOp",EDGE,"E0.3"),sQuery(id+"F2.wireOp",EDGE,"E114")])]});
            var Q27;
            Q27=makeQuery(id+"F3.opExtrude","SWEPT_EDGE",EDGE,{"disambiguationData":[OSD([sQuery(id+"F0.wireOp",EDGE,"E8.3"),sQuery(id+"F0.wireOp",EDGE,"E31.trimOffspring"),sQuery(id+"F2.wireOp",EDGE,"E114"),sQuery(id+"F2.wireOp",EDGE,"E116")])]});
            var Q28;
            Q28=makeQuery(id+"F3.opExtrude","SWEPT_EDGE",EDGE,{"disambiguationData":[OSD([sQuery(id+"F2.wireOp",EDGE,"E116"),sQuery(id+"F2.wireOp",EDGE,"E117")])]});
            var Q29;
            Q29=makeQuery(id+"F3.opExtrude","SWEPT_EDGE",EDGE,{"disambiguationData":[OSD([sQuery(id+"F0.wireOp",EDGE,"E8.4"),sQuery(id+"F0.wireOp",EDGE,"E30.trimOffspring"),sQuery(id+"F2.wireOp",EDGE,"E115"),sQuery(id+"F2.wireOp",EDGE,"E117")])]});
            var Q30;
            Q30=makeQuery(id+"F3.opExtrude","SWEPT_EDGE",EDGE,{"disambiguationData":[OSD([sQuery(id+"F0.wireOp",EDGE,"E0.4"),sQuery(id+"F2.wireOp",EDGE,"E115")])]});
            var Q31;
            Q31=makeQuery(id+"F3.opExtrude","SWEPT_EDGE",EDGE,{"disambiguationData":[OSD([sQuery(id+"F0.wireOp",EDGE,"E0.4"),sQuery(id+"F2.wireOp",EDGE,"E119")])]});
            var Q32;
            Q32=makeQuery(id+"F3.opExtrude","SWEPT_EDGE",EDGE,{"disambiguationData":[OSD([sQuery(id+"F0.wireOp",EDGE,"E8.4"),sQuery(id+"F0.wireOp",EDGE,"E32.trimOffspring"),sQuery(id+"F2.wireOp",EDGE,"E119"),sQuery(id+"F2.wireOp",EDGE,"E120")])]});
            var Q33;
            Q33=makeQuery(id+"F3.opExtrude","SWEPT_EDGE",EDGE,{"disambiguationData":[OSD([sQuery(id+"F2.wireOp",EDGE,"E120"),sQuery(id+"F2.wireOp",EDGE,"E121")])]});
            var Q34;
            Q34=makeQuery(id+"F3.opExtrude","SWEPT_EDGE",EDGE,{"disambiguationData":[OSD([sQuery(id+"F0.wireOp",EDGE,"E8.5"),sQuery(id+"F0.wireOp",EDGE,"E33.trimOffspring"),sQuery(id+"F2.wireOp",EDGE,"E118"),sQuery(id+"F2.wireOp",EDGE,"E121")])]});
            var Q35;
            Q35=makeQuery(id+"F3.opExtrude","SWEPT_EDGE",EDGE,{"disambiguationData":[OSD([sQuery(id+"F0.wireOp",EDGE,"E0.5"),sQuery(id+"F2.wireOp",EDGE,"E118")])]});
            fillet(context, id + "F4", {"entities" : qUnion([Q0, Q1, Q2, Q3, Q4, Q5, Q6, Q7, Q8, Q9, Q10, Q11, Q12, Q13, Q14, Q15, Q16, Q17, Q18, Q19, Q20, Q21, Q22, Q23, Q24, Q25, Q26, Q27, Q28, Q29, Q30, Q31, Q32, Q33, Q34, Q35]), "radius" : .5 * mm, "tangentPropagation" : true, "allowEdgeOverflow" : false});
        }
        {
            var Q0;
            Q0=makeQuery(id+"F1.opExtrude","SWEPT_EDGE",EDGE,{"disambiguationData":[OSD([sQuery(id+"F0.wireOp",EDGE,"E4.0"),sQuery(id+"F0.wireOp",EDGE,"E47.trimOffspring")])]});
            var Q1;
            Q1=makeQuery(id+"F1.opExtrude","SWEPT_EDGE",EDGE,{"disambiguationData":[OSD([sQuery(id+"F0.wireOp",EDGE,"E6.0"),sQuery(id+"F0.wireOp",EDGE,"E35.trimOffspring")])]});
            var Q2;
            Q2=makeQuery(id+"F1.opExtrude","SWEPT_EDGE",EDGE,{"disambiguationData":[OSD([sQuery(id+"F0.wireOp",EDGE,"E5.0"),sQuery(id+"F0.wireOp",EDGE,"E35.trimOffspring")])]});
            var Q3;
            Q3=makeQuery(id+"F1.opExtrude","SWEPT_EDGE",EDGE,{"disambiguationData":[OSD([sQuery(id+"F0.wireOp",EDGE,"E3.0"),sQuery(id+"F0.wireOp",EDGE,"E47.trimOffspring")])]});
            var Q4;
            Q4=makeQuery(id+"F1.opExtrude","SWEPT_EDGE",EDGE,{"disambiguationData":[OSD([sQuery(id+"F0.wireOp",EDGE,"E2.5"),sQuery(id+"F0.wireOp",EDGE,"E14")])]});
            var Q5;
            Q5=makeQuery(id+"F1.opExtrude","SWEPT_EDGE",EDGE,{"disambiguationData":[OSD([sQuery(id+"F0.wireOp",EDGE,"E2.5"),sQuery(id+"F0.wireOp",EDGE,"E13")])]});
            var Q6;
            Q6=makeQuery(id+"F1.opExtrude","SWEPT_EDGE",EDGE,{"disambiguationData":[OSD([sQuery(id+"F0.wireOp",EDGE,"E13"),sQuery(id+"F0.wireOp",EDGE,"E14")])]});
            var Q7;
            Q7=makeQuery(id+"F1.opExtrude","SWEPT_EDGE",EDGE,{"disambiguationData":[OSD([sQuery(id+"F0.wireOp",EDGE,"E6.0"),sQuery(id+"F0.wireOp",EDGE,"E48.trimOffspring")])]});
            var Q8;
            Q8=makeQuery(id+"F1.opExtrude","SWEPT_EDGE",EDGE,{"disambiguationData":[OSD([sQuery(id+"F0.wireOp",EDGE,"E4.0"),sQuery(id+"F0.wireOp",EDGE,"E60.trimOffspring")])]});
            var Q9;
            Q9=makeQuery(id+"F1.opExtrude","SWEPT_EDGE",EDGE,{"disambiguationData":[OSD([sQuery(id+"F0.wireOp",EDGE,"E5.0"),sQuery(id+"F0.wireOp",EDGE,"E48.trimOffspring")])]});
            var Q10;
            Q10=makeQuery(id+"F1.opExtrude","SWEPT_EDGE",EDGE,{"disambiguationData":[OSD([sQuery(id+"F0.wireOp",EDGE,"E3.0"),sQuery(id+"F0.wireOp",EDGE,"E60.trimOffspring")])]});
            var Q11;
            Q11=makeQuery(id+"F1.opExtrude","SWEPT_EDGE",EDGE,{"disambiguationData":[OSD([sQuery(id+"F0.wireOp",EDGE,"E2.4"),sQuery(id+"F0.wireOp",EDGE,"E15")])]});
            var Q12;
            Q12=makeQuery(id+"F1.opExtrude","SWEPT_EDGE",EDGE,{"disambiguationData":[OSD([sQuery(id+"F0.wireOp",EDGE,"E2.4"),sQuery(id+"F0.wireOp",EDGE,"E16")])]});
            var Q13;
            Q13=makeQuery(id+"F1.opExtrude","SWEPT_EDGE",EDGE,{"disambiguationData":[OSD([sQuery(id+"F0.wireOp",EDGE,"E15"),sQuery(id+"F0.wireOp",EDGE,"E16")])]});
            var Q14;
            Q14=makeQuery(id+"F1.opExtrude","SWEPT_EDGE",EDGE,{"disambiguationData":[OSD([sQuery(id+"F0.wireOp",EDGE,"E8.3"),sQuery(id+"F0.wireOp",EDGE,"E31.trimOffspring")])]});
            var Q15;
            Q15=makeQuery(id+"F1.opExtrude","SWEPT_EDGE",EDGE,{"disambiguationData":[OSD([sQuery(id+"F0.wireOp",EDGE,"E6.3"),sQuery(id+"F0.wireOp",EDGE,"E42.trimOffspring")])]});
            var Q16;
            Q16=makeQuery(id+"F1.opExtrude","SWEPT_EDGE",EDGE,{"disambiguationData":[OSD([sQuery(id+"F0.wireOp",EDGE,"E4.3"),sQuery(id+"F0.wireOp",EDGE,"E54.trimOffspring")])]});
            var Q17;
            Q17=makeQuery(id+"F1.opExtrude","SWEPT_EDGE",EDGE,{"disambiguationData":[OSD([sQuery(id+"F0.wireOp",EDGE,"E2.3"),sQuery(id+"F0.wireOp",EDGE,"E17")])]});
            var Q18;
            Q18=makeQuery(id+"F1.opExtrude","SWEPT_EDGE",EDGE,{"disambiguationData":[OSD([sQuery(id+"F0.wireOp",EDGE,"E3.3"),sQuery(id+"F0.wireOp",EDGE,"E65.trimOffspring")])]});
            var Q19;
            Q19=makeQuery(id+"F1.opExtrude","SWEPT_EDGE",EDGE,{"disambiguationData":[OSD([sQuery(id+"F0.wireOp",EDGE,"E5.3"),sQuery(id+"F0.wireOp",EDGE,"E53.trimOffspring")])]});
            var Q20;
            Q20=makeQuery(id+"F1.opExtrude","SWEPT_EDGE",EDGE,{"disambiguationData":[OSD([sQuery(id+"F0.wireOp",EDGE,"E7.3"),sQuery(id+"F0.wireOp",EDGE,"E41.trimOffspring")])]});
            var Q21;
            Q21=makeQuery(id+"F1.opExtrude","SWEPT_EDGE",EDGE,{"disambiguationData":[OSD([sQuery(id+"F0.wireOp",EDGE,"E8.3"),sQuery(id+"F0.wireOp",EDGE,"E41.trimOffspring")])]});
            var Q22;
            Q22=makeQuery(id+"F1.opExtrude","SWEPT_EDGE",EDGE,{"disambiguationData":[OSD([sQuery(id+"F0.wireOp",EDGE,"E4.3"),sQuery(id+"F0.wireOp",EDGE,"E65.trimOffspring")])]});
            var Q23;
            Q23=makeQuery(id+"F1.opExtrude","SWEPT_EDGE",EDGE,{"disambiguationData":[OSD([sQuery(id+"F0.wireOp",EDGE,"E2.3"),sQuery(id+"F0.wireOp",EDGE,"E18")])]});
            var Q24;
            Q24=makeQuery(id+"F1.opExtrude","SWEPT_EDGE",EDGE,{"disambiguationData":[OSD([sQuery(id+"F0.wireOp",EDGE,"E6.4"),sQuery(id+"F0.wireOp",EDGE,"E43.trimOffspring")])]});
            var Q25;
            Q25=makeQuery(id+"F1.opExtrude","SWEPT_EDGE",EDGE,{"disambiguationData":[OSD([sQuery(id+"F0.wireOp",EDGE,"E8.4"),sQuery(id+"F0.wireOp",EDGE,"E30.trimOffspring")])]});
            var Q26;
            Q26=makeQuery(id+"F1.opExtrude","SWEPT_EDGE",EDGE,{"disambiguationData":[OSD([sQuery(id+"F0.wireOp",EDGE,"E3.4"),sQuery(id+"F0.wireOp",EDGE,"E55.trimOffspring")])]});
            var Q27;
            Q27=makeQuery(id+"F1.opExtrude","SWEPT_EDGE",EDGE,{"disambiguationData":[OSD([sQuery(id+"F0.wireOp",EDGE,"E5.4"),sQuery(id+"F0.wireOp",EDGE,"E43.trimOffspring")])]});
            var Q28;
            Q28=makeQuery(id+"F1.opExtrude","SWEPT_EDGE",EDGE,{"disambiguationData":[OSD([sQuery(id+"F0.wireOp",EDGE,"E7.4"),sQuery(id+"F0.wireOp",EDGE,"E30.trimOffspring")])]});
            var Q29;
            Q29=makeQuery(id+"F1.opExtrude","SWEPT_EDGE",EDGE,{"disambiguationData":[OSD([sQuery(id+"F0.wireOp",EDGE,"E7.4"),sQuery(id+"F0.wireOp",EDGE,"E32.trimOffspring")])]});
            var Q30;
            Q30=makeQuery(id+"F1.opExtrude","SWEPT_EDGE",EDGE,{"disambiguationData":[OSD([sQuery(id+"F0.wireOp",EDGE,"E5.4"),sQuery(id+"F0.wireOp",EDGE,"E44.trimOffspring")])]});
            var Q31;
            Q31=makeQuery(id+"F1.opExtrude","SWEPT_EDGE",EDGE,{"disambiguationData":[OSD([sQuery(id+"F0.wireOp",EDGE,"E3.4"),sQuery(id+"F0.wireOp",EDGE,"E56.trimOffspring")])]});
            var Q32;
            Q32=makeQuery(id+"F1.opExtrude","SWEPT_EDGE",EDGE,{"disambiguationData":[OSD([sQuery(id+"F0.wireOp",EDGE,"E8.4"),sQuery(id+"F0.wireOp",EDGE,"E32.trimOffspring")])]});
            var Q33;
            Q33=makeQuery(id+"F1.opExtrude","SWEPT_EDGE",EDGE,{"disambiguationData":[OSD([sQuery(id+"F0.wireOp",EDGE,"E6.4"),sQuery(id+"F0.wireOp",EDGE,"E44.trimOffspring")])]});
            var Q34;
            Q34=makeQuery(id+"F1.opExtrude","SWEPT_EDGE",EDGE,{"disambiguationData":[OSD([sQuery(id+"F0.wireOp",EDGE,"E4.4"),sQuery(id+"F0.wireOp",EDGE,"E56.trimOffspring")])]});
            var Q35;
            Q35=makeQuery(id+"F1.opExtrude","SWEPT_EDGE",EDGE,{"disambiguationData":[OSD([sQuery(id+"F0.wireOp",EDGE,"E2.2"),sQuery(id+"F0.wireOp",EDGE,"E20")])]});
            var Q36;
            Q36=makeQuery(id+"F1.opExtrude","SWEPT_EDGE",EDGE,{"disambiguationData":[OSD([sQuery(id+"F0.wireOp",EDGE,"E4.2"),sQuery(id+"F0.wireOp",EDGE,"E63.trimOffspring")])]});
            var Q37;
            Q37=makeQuery(id+"F1.opExtrude","SWEPT_EDGE",EDGE,{"disambiguationData":[OSD([sQuery(id+"F0.wireOp",EDGE,"E6.2"),sQuery(id+"F0.wireOp",EDGE,"E51.trimOffspring")])]});
            var Q38;
            Q38=makeQuery(id+"F1.opExtrude","SWEPT_EDGE",EDGE,{"disambiguationData":[OSD([sQuery(id+"F0.wireOp",EDGE,"E8.2"),sQuery(id+"F0.wireOp",EDGE,"E39.trimOffspring")])]});
            var Q39;
            Q39=makeQuery(id+"F1.opExtrude","SWEPT_EDGE",EDGE,{"disambiguationData":[OSD([sQuery(id+"F0.wireOp",EDGE,"E19"),sQuery(id+"F0.wireOp",EDGE,"E20")])]});
            var Q40;
            Q40=makeQuery(id+"F1.opExtrude","SWEPT_EDGE",EDGE,{"disambiguationData":[OSD([sQuery(id+"F0.wireOp",EDGE,"E3.2"),sQuery(id+"F0.wireOp",EDGE,"E63.trimOffspring")])]});
            var Q41;
            Q41=makeQuery(id+"F1.opExtrude","SWEPT_EDGE",EDGE,{"disambiguationData":[OSD([sQuery(id+"F0.wireOp",EDGE,"E5.2"),sQuery(id+"F0.wireOp",EDGE,"E51.trimOffspring")])]});
            var Q42;
            Q42=makeQuery(id+"F1.opExtrude","SWEPT_EDGE",EDGE,{"disambiguationData":[OSD([sQuery(id+"F0.wireOp",EDGE,"E7.2"),sQuery(id+"F0.wireOp",EDGE,"E39.trimOffspring")])]});
            var Q43;
            Q43=makeQuery(id+"F1.opExtrude","SWEPT_EDGE",EDGE,{"disambiguationData":[OSD([sQuery(id+"F0.wireOp",EDGE,"E8.2"),sQuery(id+"F0.wireOp",EDGE,"E40.trimOffspring")])]});
            var Q44;
            Q44=makeQuery(id+"F1.opExtrude","SWEPT_EDGE",EDGE,{"disambiguationData":[OSD([sQuery(id+"F0.wireOp",EDGE,"E6.2"),sQuery(id+"F0.wireOp",EDGE,"E52.trimOffspring")])]});
            var Q45;
            Q45=makeQuery(id+"F1.opExtrude","SWEPT_EDGE",EDGE,{"disambiguationData":[OSD([sQuery(id+"F0.wireOp",EDGE,"E4.2"),sQuery(id+"F0.wireOp",EDGE,"E64.trimOffspring")])]});
            var Q46;
            Q46=makeQuery(id+"F1.opExtrude","SWEPT_EDGE",EDGE,{"disambiguationData":[OSD([sQuery(id+"F0.wireOp",EDGE,"E2.2"),sQuery(id+"F0.wireOp",EDGE,"E19")])]});
            var Q47;
            Q47=makeQuery(id+"F1.opExtrude","SWEPT_EDGE",EDGE,{"disambiguationData":[OSD([sQuery(id+"F0.wireOp",EDGE,"E5.2"),sQuery(id+"F0.wireOp",EDGE,"E52.trimOffspring")])]});
            var Q48;
            Q48=makeQuery(id+"F1.opExtrude","SWEPT_EDGE",EDGE,{"disambiguationData":[OSD([sQuery(id+"F0.wireOp",EDGE,"E17"),sQuery(id+"F0.wireOp",EDGE,"E18")])]});
            var Q49;
            Q49=makeQuery(id+"F1.opExtrude","SWEPT_EDGE",EDGE,{"disambiguationData":[OSD([sQuery(id+"F0.wireOp",EDGE,"E2.0"),sQuery(id+"F0.wireOp",EDGE,"E59.trimOffspring")])]});
            var Q50;
            Q50=makeQuery(id+"F1.opExtrude","SWEPT_EDGE",EDGE,{"disambiguationData":[OSD([sQuery(id+"F0.wireOp",EDGE,"E12"),sQuery(id+"F0.wireOp",EDGE,"E80")])]});
            var Q51;
            Q51=makeQuery(id+"F1.opExtrude","SWEPT_EDGE",EDGE,{"disambiguationData":[OSD([sQuery(id+"F0.wireOp",EDGE,"E4.5"),sQuery(id+"F0.wireOp",EDGE,"E58.trimOffspring")])]});
            var Q52;
            Q52=makeQuery(id+"F1.opExtrude","SWEPT_EDGE",EDGE,{"disambiguationData":[OSD([sQuery(id+"F0.wireOp",EDGE,"E6.5"),sQuery(id+"F0.wireOp",EDGE,"E46.trimOffspring")])]});
            var Q53;
            Q53=makeQuery(id+"F1.opExtrude","SWEPT_EDGE",EDGE,{"disambiguationData":[OSD([sQuery(id+"F0.wireOp",EDGE,"E8.5"),sQuery(id+"F0.wireOp",EDGE,"E34.trimOffspring")])]});
            var Q54;
            Q54=makeQuery(id+"F1.opExtrude","SWEPT_EDGE",EDGE,{"disambiguationData":[OSD([sQuery(id+"F0.wireOp",EDGE,"E8.5"),sQuery(id+"F0.wireOp",EDGE,"E33.trimOffspring")])]});
            var Q55;
            Q55=makeQuery(id+"F1.opExtrude","SWEPT_EDGE",EDGE,{"disambiguationData":[OSD([sQuery(id+"F0.wireOp",EDGE,"E6.5"),sQuery(id+"F0.wireOp",EDGE,"E45.trimOffspring")])]});
            var Q56;
            Q56=makeQuery(id+"F1.opExtrude","SWEPT_EDGE",EDGE,{"disambiguationData":[OSD([sQuery(id+"F0.wireOp",EDGE,"E4.5"),sQuery(id+"F0.wireOp",EDGE,"E57.trimOffspring")])]});
            var Q57;
            Q57=makeQuery(id+"F1.opExtrude","SWEPT_EDGE",EDGE,{"disambiguationData":[OSD([sQuery(id+"F0.wireOp",EDGE,"E7.5"),sQuery(id+"F0.wireOp",EDGE,"E33.trimOffspring")])]});
            var Q58;
            Q58=makeQuery(id+"F1.opExtrude","SWEPT_EDGE",EDGE,{"disambiguationData":[OSD([sQuery(id+"F0.wireOp",EDGE,"E5.5"),sQuery(id+"F0.wireOp",EDGE,"E45.trimOffspring")])]});
            var Q59;
            Q59=makeQuery(id+"F1.opExtrude","SWEPT_EDGE",EDGE,{"disambiguationData":[OSD([sQuery(id+"F0.wireOp",EDGE,"E3.5"),sQuery(id+"F0.wireOp",EDGE,"E57.trimOffspring")])]});
            var Q60;
            Q60=makeQuery(id+"F1.opExtrude","SWEPT_EDGE",EDGE,{"disambiguationData":[OSD([sQuery(id+"F0.wireOp",EDGE,"E3.5"),sQuery(id+"F0.wireOp",EDGE,"E58.trimOffspring")])]});
            var Q61;
            Q61=makeQuery(id+"F1.opExtrude","SWEPT_EDGE",EDGE,{"disambiguationData":[OSD([sQuery(id+"F0.wireOp",EDGE,"E5.5"),sQuery(id+"F0.wireOp",EDGE,"E46.trimOffspring")])]});
            var Q62;
            Q62=makeQuery(id+"F1.opExtrude","SWEPT_EDGE",EDGE,{"disambiguationData":[OSD([sQuery(id+"F0.wireOp",EDGE,"E7.5"),sQuery(id+"F0.wireOp",EDGE,"E34.trimOffspring")])]});
            var Q63;
            Q63=makeQuery(id+"F1.opExtrude","SWEPT_EDGE",EDGE,{"disambiguationData":[OSD([sQuery(id+"F0.wireOp",EDGE,"E4.4"),sQuery(id+"F0.wireOp",EDGE,"E55.trimOffspring")])]});
            var Q64;
            Q64=makeQuery(id+"F1.opExtrude","SWEPT_EDGE",EDGE,{"disambiguationData":[OSD([sQuery(id+"F0.wireOp",EDGE,"E7.0"),sQuery(id+"F0.wireOp",EDGE,"E36.trimOffspring")])]});
            var Q65;
            Q65=makeQuery(id+"F1.opExtrude","SWEPT_EDGE",EDGE,{"disambiguationData":[OSD([sQuery(id+"F0.wireOp",EDGE,"E7.0"),sQuery(id+"F0.wireOp",EDGE,"E12")])]});
            var Q66;
            Q66=makeQuery(id+"F1.opExtrude","SWEPT_EDGE",EDGE,{"disambiguationData":[OSD([sQuery(id+"F0.wireOp",EDGE,"E8.1"),sQuery(id+"F0.wireOp",EDGE,"E37.trimOffspring")])]});
            var Q67;
            Q67=makeQuery(id+"F1.opExtrude","SWEPT_EDGE",EDGE,{"disambiguationData":[OSD([sQuery(id+"F0.wireOp",EDGE,"E6.1"),sQuery(id+"F0.wireOp",EDGE,"E49.trimOffspring")])]});
            var Q68;
            Q68=makeQuery(id+"F1.opExtrude","SWEPT_EDGE",EDGE,{"disambiguationData":[OSD([sQuery(id+"F0.wireOp",EDGE,"E4.1"),sQuery(id+"F0.wireOp",EDGE,"E61.trimOffspring")])]});
            var Q69;
            Q69=makeQuery(id+"F1.opExtrude","SWEPT_EDGE",EDGE,{"disambiguationData":[OSD([sQuery(id+"F0.wireOp",EDGE,"E2.1"),sQuery(id+"F0.wireOp",EDGE,"E9")])]});
            var Q70;
            Q70=makeQuery(id+"F1.opExtrude","SWEPT_EDGE",EDGE,{"disambiguationData":[OSD([sQuery(id+"F0.wireOp",EDGE,"E7.1"),sQuery(id+"F0.wireOp",EDGE,"E37.trimOffspring")])]});
            var Q71;
            Q71=makeQuery(id+"F1.opExtrude","SWEPT_EDGE",EDGE,{"disambiguationData":[OSD([sQuery(id+"F0.wireOp",EDGE,"E5.1"),sQuery(id+"F0.wireOp",EDGE,"E49.trimOffspring")])]});
            var Q72;
            Q72=makeQuery(id+"F1.opExtrude","SWEPT_EDGE",EDGE,{"disambiguationData":[OSD([sQuery(id+"F0.wireOp",EDGE,"E3.1"),sQuery(id+"F0.wireOp",EDGE,"E61.trimOffspring")])]});
            var Q73;
            Q73=makeQuery(id+"F1.opExtrude","SWEPT_EDGE",EDGE,{"disambiguationData":[OSD([sQuery(id+"F0.wireOp",EDGE,"E9"),sQuery(id+"F0.wireOp",EDGE,"E10")])]});
            var Q74;
            Q74=makeQuery(id+"F1.opExtrude","SWEPT_EDGE",EDGE,{"disambiguationData":[OSD([sQuery(id+"F0.wireOp",EDGE,"E8.1"),sQuery(id+"F0.wireOp",EDGE,"E38.trimOffspring")])]});
            var Q75;
            Q75=makeQuery(id+"F1.opExtrude","SWEPT_EDGE",EDGE,{"disambiguationData":[OSD([sQuery(id+"F0.wireOp",EDGE,"E6.1"),sQuery(id+"F0.wireOp",EDGE,"E50.trimOffspring")])]});
            var Q76;
            Q76=makeQuery(id+"F1.opExtrude","SWEPT_EDGE",EDGE,{"disambiguationData":[OSD([sQuery(id+"F0.wireOp",EDGE,"E4.1"),sQuery(id+"F0.wireOp",EDGE,"E62.trimOffspring")])]});
            var Q77;
            Q77=makeQuery(id+"F1.opExtrude","SWEPT_EDGE",EDGE,{"disambiguationData":[OSD([sQuery(id+"F0.wireOp",EDGE,"E2.1"),sQuery(id+"F0.wireOp",EDGE,"E10")])]});
            var Q78;
            Q78=makeQuery(id+"F1.opExtrude","SWEPT_EDGE",EDGE,{"disambiguationData":[OSD([sQuery(id+"F0.wireOp",EDGE,"E7.1"),sQuery(id+"F0.wireOp",EDGE,"E38.trimOffspring")])]});
            var Q79;
            Q79=makeQuery(id+"F1.opExtrude","SWEPT_EDGE",EDGE,{"disambiguationData":[OSD([sQuery(id+"F0.wireOp",EDGE,"E5.1"),sQuery(id+"F0.wireOp",EDGE,"E50.trimOffspring")])]});
            var Q80;
            Q80=makeQuery(id+"F1.opExtrude","SWEPT_EDGE",EDGE,{"disambiguationData":[OSD([sQuery(id+"F0.wireOp",EDGE,"E3.1"),sQuery(id+"F0.wireOp",EDGE,"E62.trimOffspring")])]});
            var Q81;
            Q81=makeQuery(id+"F1.opExtrude","SWEPT_EDGE",EDGE,{"disambiguationData":[OSD([sQuery(id+"F0.wireOp",EDGE,"E3.2"),sQuery(id+"F0.wireOp",EDGE,"E64.trimOffspring")])]});
            var Q82;
            Q82=makeQuery(id+"F1.opExtrude","SWEPT_EDGE",EDGE,{"disambiguationData":[OSD([sQuery(id+"F0.wireOp",EDGE,"E3.3"),sQuery(id+"F0.wireOp",EDGE,"E54.trimOffspring")])]});
            var Q83;
            Q83=makeQuery(id+"F1.opExtrude","SWEPT_EDGE",EDGE,{"disambiguationData":[OSD([sQuery(id+"F0.wireOp",EDGE,"E6.3"),sQuery(id+"F0.wireOp",EDGE,"E53.trimOffspring")])]});
            var Q84;
            Q84=makeQuery(id+"F1.opExtrude","SWEPT_EDGE",EDGE,{"disambiguationData":[OSD([sQuery(id+"F0.wireOp",EDGE,"E5.3"),sQuery(id+"F0.wireOp",EDGE,"E42.trimOffspring")])]});
            var Q85;
            Q85=makeQuery(id+"F1.opExtrude","SWEPT_EDGE",EDGE,{"disambiguationData":[OSD([sQuery(id+"F0.wireOp",EDGE,"E7.3"),sQuery(id+"F0.wireOp",EDGE,"E31.trimOffspring")])]});
            var Q86;
            Q86=makeQuery(id+"F1.opExtrude","SWEPT_EDGE",EDGE,{"disambiguationData":[OSD([sQuery(id+"F0.wireOp",EDGE,"E2.0"),sQuery(id+"F0.wireOp",EDGE,"E11")])]});
            var Q87;
            Q87=makeQuery(id+"F3.opExtrude","SWEPT_EDGE",EDGE,{"disambiguationData":[OSD([sQuery(id+"F0.wireOp",EDGE,"E0.0"),sQuery(id+"F2.wireOp",EDGE,"E102")])]});
            var Q88;
            Q88=makeQuery(id+"F3.opExtrude","SWEPT_EDGE",EDGE,{"disambiguationData":[OSD([sQuery(id+"F0.wireOp",EDGE,"E0.1"),sQuery(id+"F2.wireOp",EDGE,"E103")])]});
            var Q89;
            Q89=makeQuery(id+"F3.opExtrude","SWEPT_EDGE",EDGE,{"disambiguationData":[OSD([sQuery(id+"F0.wireOp",EDGE,"E36.trimOffspring"),sQuery(id+"F0.wireOp",EDGE,"E80"),sQuery(id+"F2.wireOp",EDGE,"E102"),sQuery(id+"F2.wireOp",EDGE,"E104")])]});
            fillet(context, id + "F5", {"entities" : qUnion([Q0, Q1, Q2, Q3, Q4, Q5, Q6, Q7, Q8, Q9, Q10, Q11, Q12, Q13, Q14, Q15, Q16, Q17, Q18, Q19, Q20, Q21, Q22, Q23, Q24, Q25, Q26, Q27, Q28, Q29, Q30, Q31, Q32, Q33, Q34, Q35, Q36, Q37, Q38, Q39, Q40, Q41, Q42, Q43, Q44, Q45, Q46, Q47, Q48, Q49, Q50, Q51, Q52, Q53, Q54, Q55, Q56, Q57, Q58, Q59, Q60, Q61, Q62, Q63, Q64, Q65, Q66, Q67, Q68, Q69, Q70, Q71, Q72, Q73, Q74, Q75, Q76, Q77, Q78, Q79, Q80, Q81, Q82, Q83, Q84, Q85, Q86, Q87, Q88, Q89]), "radius" : .5 * mm, "tangentPropagation" : true, "allowEdgeOverflow" : false});
        }
        {
            var Q0;
            Q0=makeQuery(id+"F3.opExtrude","CAP_FACE",FACE,{"disambiguationData":[OSD([sQuery(id+"F0.wireOp",EDGE,"E0.2"),sQuery(id+"F0.wireOp",EDGE,"E0.3"),sQuery(id+"F2.wireOp",EDGE,"E110"),sQuery(id+"F2.wireOp",EDGE,"E111"),sQuery(id+"F2.wireOp",EDGE,"E112"),sQuery(id+"F2.wireOp",EDGE,"E113")])],"isStart":false});
            var Q1;
            Q1=makeQuery(id+"F3.opExtrude","CAP_FACE",FACE,{"disambiguationData":[OSD([sQuery(id+"F2.wireOp",EDGE,"E126.0"),sQuery(id+"F2.wireOp",EDGE,"E126.1"),sQuery(id+"F2.wireOp",EDGE,"E126.2"),sQuery(id+"F2.wireOp",EDGE,"E126.3"),sQuery(id+"F2.wireOp",EDGE,"E126.4"),sQuery(id+"F2.wireOp",EDGE,"E126.5")])],"isStart":false});
            var Q2;
            Q2=makeQuery(id+"F3.opExtrude","CAP_FACE",FACE,{"disambiguationData":[OSD([sQuery(id+"F0.wireOp",EDGE,"E0.1"),sQuery(id+"F0.wireOp",EDGE,"E0.2"),sQuery(id+"F2.wireOp",EDGE,"E106"),sQuery(id+"F2.wireOp",EDGE,"E107"),sQuery(id+"F2.wireOp",EDGE,"E108"),sQuery(id+"F2.wireOp",EDGE,"E109")])],"isStart":false});
            var Q3;
            Q3=makeQuery(id+"F3.opExtrude","CAP_FACE",FACE,{"disambiguationData":[OSD([sQuery(id+"F0.wireOp",EDGE,"E0.0"),sQuery(id+"F0.wireOp",EDGE,"E0.1"),sQuery(id+"F2.wireOp",EDGE,"E102"),sQuery(id+"F2.wireOp",EDGE,"E103"),sQuery(id+"F2.wireOp",EDGE,"E104"),sQuery(id+"F2.wireOp",EDGE,"E105")])],"isStart":false});
            var Q4;
            Q4=makeQuery(id+"F3.opExtrude","CAP_FACE",FACE,{"disambiguationData":[OSD([sQuery(id+"F0.wireOp",EDGE,"E0.0"),sQuery(id+"F0.wireOp",EDGE,"E0.5"),sQuery(id+"F2.wireOp",EDGE,"E122"),sQuery(id+"F2.wireOp",EDGE,"E123"),sQuery(id+"F2.wireOp",EDGE,"E124"),sQuery(id+"F2.wireOp",EDGE,"E125")])],"isStart":false});
            var Q5;
            Q5=makeQuery(id+"F3.opExtrude","CAP_FACE",FACE,{"disambiguationData":[OSD([sQuery(id+"F0.wireOp",EDGE,"E0.3"),sQuery(id+"F0.wireOp",EDGE,"E0.4"),sQuery(id+"F2.wireOp",EDGE,"E114"),sQuery(id+"F2.wireOp",EDGE,"E115"),sQuery(id+"F2.wireOp",EDGE,"E116"),sQuery(id+"F2.wireOp",EDGE,"E117")])],"isStart":false});
            var Q6;
            Q6=makeQuery(id+"F3.opExtrude","CAP_FACE",FACE,{"disambiguationData":[OSD([sQuery(id+"F0.wireOp",EDGE,"E0.4"),sQuery(id+"F0.wireOp",EDGE,"E0.5"),sQuery(id+"F2.wireOp",EDGE,"E118"),sQuery(id+"F2.wireOp",EDGE,"E119"),sQuery(id+"F2.wireOp",EDGE,"E120"),sQuery(id+"F2.wireOp",EDGE,"E121")])],"isStart":false});
            chamfer(context, id + "F6", {"entities" : qUnion([Q0, Q1, Q2, Q3, Q4, Q5, Q6]), "width" : .5 * mm, "tangentPropagation" : true});
        }
        {
            var Q0;
            Q0=makeQuery(id+"F1.opExtrude","CAP_FACE",FACE,{"disambiguationData":[OSD([sQuery(id+"F0.wireOp",EDGE,"E0.0"),sQuery(id+"F0.wireOp",EDGE,"E0.1"),sQuery(id+"F0.wireOp",EDGE,"E0.2"),sQuery(id+"F0.wireOp",EDGE,"E0.3"),sQuery(id+"F0.wireOp",EDGE,"E0.4"),sQuery(id+"F0.wireOp",EDGE,"E0.5"),sQuery(id+"F0.wireOp",EDGE,"E2.0"),sQuery(id+"F0.wireOp",EDGE,"E2.1"),sQuery(id+"F0.wireOp",EDGE,"E2.2"),sQuery(id+"F0.wireOp",EDGE,"E2.3"),sQuery(id+"F0.wireOp",EDGE,"E2.4"),sQuery(id+"F0.wireOp",EDGE,"E2.5"),sQuery(id+"F0.wireOp",EDGE,"E3.0"),sQuery(id+"F0.wireOp",EDGE,"E3.1"),sQuery(id+"F0.wireOp",EDGE,"E3.2"),sQuery(id+"F0.wireOp",EDGE,"E3.3"),sQuery(id+"F0.wireOp",EDGE,"E3.4"),sQuery(id+"F0.wireOp",EDGE,"E3.5"),sQuery(id+"F0.wireOp",EDGE,"E4.0"),sQuery(id+"F0.wireOp",EDGE,"E4.1"),sQuery(id+"F0.wireOp",EDGE,"E4.2"),sQuery(id+"F0.wireOp",EDGE,"E4.3"),sQuery(id+"F0.wireOp",EDGE,"E4.4"),sQuery(id+"F0.wireOp",EDGE,"E4.5"),sQuery(id+"F0.wireOp",EDGE,"E5.0"),sQuery(id+"F0.wireOp",EDGE,"E5.1"),sQuery(id+"F0.wireOp",EDGE,"E5.2"),sQuery(id+"F0.wireOp",EDGE,"E5.3"),sQuery(id+"F0.wireOp",EDGE,"E5.4"),sQuery(id+"F0.wireOp",EDGE,"E5.5"),sQuery(id+"F0.wireOp",EDGE,"E6.0"),sQuery(id+"F0.wireOp",EDGE,"E6.1"),sQuery(id+"F0.wireOp",EDGE,"E6.2"),sQuery(id+"F0.wireOp",EDGE,"E6.3"),sQuery(id+"F0.wireOp",EDGE,"E6.4"),sQuery(id+"F0.wireOp",EDGE,"E6.5"),sQuery(id+"F0.wireOp",EDGE,"E7.0"),sQuery(id+"F0.wireOp",EDGE,"E7.1"),sQuery(id+"F0.wireOp",EDGE,"E7.2"),sQuery(id+"F0.wireOp",EDGE,"E7.3"),sQuery(id+"F0.wireOp",EDGE,"E7.4"),sQuery(id+"F0.wireOp",EDGE,"E7.5"),sQuery(id+"F0.wireOp",EDGE,"E8.1"),sQuery(id+"F0.wireOp",EDGE,"E8.2"),sQuery(id+"F0.wireOp",EDGE,"E8.3"),sQuery(id+"F0.wireOp",EDGE,"E8.4"),sQuery(id+"F0.wireOp",EDGE,"E8.5"),sQuery(id+"F0.wireOp",EDGE,"E9"),sQuery(id+"F0.wireOp",EDGE,"E10"),sQuery(id+"F0.wireOp",EDGE,"E11"),sQuery(id+"F0.wireOp",EDGE,"E12"),sQuery(id+"F0.wireOp",EDGE,"E13"),sQuery(id+"F0.wireOp",EDGE,"E14"),sQuery(id+"F0.wireOp",EDGE,"E15"),sQuery(id+"F0.wireOp",EDGE,"E16"),sQuery(id+"F0.wireOp",EDGE,"E17"),sQuery(id+"F0.wireOp",EDGE,"E18"),sQuery(id+"F0.wireOp",EDGE,"E19"),sQuery(id+"F0.wireOp",EDGE,"E20"),sQuery(id+"F0.wireOp",EDGE,"E30.trimOffspring"),sQuery(id+"F0.wireOp",EDGE,"E31.trimOffspring"),sQuery(id+"F0.wireOp",EDGE,"E32.trimOffspring"),sQuery(id+"F0.wireOp",EDGE,"E33.trimOffspring"),sQuery(id+"F0.wireOp",EDGE,"E34.trimOffspring"),sQuery(id+"F0.wireOp",EDGE,"E35.trimOffspring"),sQuery(id+"F0.wireOp",EDGE,"E36.trimOffspring"),sQuery(id+"F0.wireOp",EDGE,"E37.trimOffspring"),sQuery(id+"F0.wireOp",EDGE,"E38.trimOffspring"),sQuery(id+"F0.wireOp",EDGE,"E39.trimOffspring"),sQuery(id+"F0.wireOp",EDGE,"E40.trimOffspring"),sQuery(id+"F0.wireOp",EDGE,"E41.trimOffspring"),sQuery(id+"F0.wireOp",EDGE,"E42.trimOffspring"),sQuery(id+"F0.wireOp",EDGE,"E43.trimOffspring"),sQuery(id+"F0.wireOp",EDGE,"E44.trimOffspring"),sQuery(id+"F0.wireOp",EDGE,"E45.trimOffspring"),sQuery(id+"F0.wireOp",EDGE,"E46.trimOffspring"),sQuery(id+"F0.wireOp",EDGE,"E47.trimOffspring"),sQuery(id+"F0.wireOp",EDGE,"E48.trimOffspring"),sQuery(id+"F0.wireOp",EDGE,"E49.trimOffspring"),sQuery(id+"F0.wireOp",EDGE,"E50.trimOffspring"),sQuery(id+"F0.wireOp",EDGE,"E51.trimOffspring"),sQuery(id+"F0.wireOp",EDGE,"E52.trimOffspring"),sQuery(id+"F0.wireOp",EDGE,"E53.trimOffspring"),sQuery(id+"F0.wireOp",EDGE,"E54.trimOffspring"),sQuery(id+"F0.wireOp",EDGE,"E55.trimOffspring"),sQuery(id+"F0.wireOp",EDGE,"E56.trimOffspring"),sQuery(id+"F0.wireOp",EDGE,"E57.trimOffspring"),sQuery(id+"F0.wireOp",EDGE,"E58.trimOffspring"),sQuery(id+"F0.wireOp",EDGE,"E59.trimOffspring"),sQuery(id+"F0.wireOp",EDGE,"E60.trimOffspring"),sQuery(id+"F0.wireOp",EDGE,"E61.trimOffspring"),sQuery(id+"F0.wireOp",EDGE,"E62.trimOffspring"),sQuery(id+"F0.wireOp",EDGE,"E63.trimOffspring"),sQuery(id+"F0.wireOp",EDGE,"E64.trimOffspring"),sQuery(id+"F0.wireOp",EDGE,"E65.trimOffspring"),sQuery(id+"F0.wireOp",EDGE,"E80")])],"isStart":false});
            chamfer(context, id + "F7", {"entities" : qUnion([Q0]), "width" : 1 * mm, "tangentPropagation" : true});
        }
        {
            var Q0;
            Q0=makeQuery(id+"F1.opExtrude","CAP_EDGE",EDGE,{"disambiguationData":[OSD([sQuery(id+"F0.wireOp",EDGE,"E0.1")])],"isStart":true});
            var Q1;
            Q1=makeQuery(id+"F1.opExtrude","CAP_EDGE",EDGE,{"disambiguationData":[OSD([sQuery(id+"F0.wireOp",EDGE,"E0.0")])],"isStart":true});
            var Q2;
            Q2=makeQuery(id+"F1.opExtrude","CAP_EDGE",EDGE,{"disambiguationData":[OSD([sQuery(id+"F0.wireOp",EDGE,"E0.5")])],"isStart":true});
            var Q3;
            Q3=makeQuery(id+"F1.opExtrude","CAP_EDGE",EDGE,{"disambiguationData":[OSD([sQuery(id+"F0.wireOp",EDGE,"E0.4")])],"isStart":true});
            var Q4;
            Q4=makeQuery(id+"F1.opExtrude","CAP_EDGE",EDGE,{"disambiguationData":[OSD([sQuery(id+"F0.wireOp",EDGE,"E0.3")])],"isStart":true});
            var Q5;
            Q5=makeQuery(id+"F1.opExtrude","CAP_EDGE",EDGE,{"disambiguationData":[OSD([sQuery(id+"F0.wireOp",EDGE,"E0.2")])],"isStart":true});
            var Q6;
            Q6=makeQuery(id+"F1.opExtrude","CAP_EDGE",EDGE,{"disambiguationData":[OSD([sQuery(id+"F0.wireOp",EDGE,"E8.2")])],"isStart":true});
            var Q7;
            Q7=makeQuery(id+"F1.opExtrude","CAP_EDGE",EDGE,{"disambiguationData":[OSD([sQuery(id+"F0.wireOp",EDGE,"E7.1")])],"isStart":true});
            var Q8;
            Q8=makeQuery(id+"F1.opExtrude","CAP_EDGE",EDGE,{"disambiguationData":[OSD([sQuery(id+"F0.wireOp",EDGE,"E6.1")])],"isStart":true});
            var Q9;
            Q9=makeQuery(id+"F1.opExtrude","CAP_EDGE",EDGE,{"disambiguationData":[OSD([sQuery(id+"F0.wireOp",EDGE,"E6.2")])],"isStart":true});
            var Q10;
            Q10=makeQuery(id+"F1.opExtrude","CAP_EDGE",EDGE,{"disambiguationData":[OSD([sQuery(id+"F0.wireOp",EDGE,"E7.3")])],"isStart":true});
            var Q11;
            Q11=makeQuery(id+"F1.opExtrude","CAP_EDGE",EDGE,{"disambiguationData":[OSD([sQuery(id+"F0.wireOp",EDGE,"E7.4")])],"isStart":true});
            var Q12;
            Q12=makeQuery(id+"F1.opExtrude","CAP_EDGE",EDGE,{"disambiguationData":[OSD([sQuery(id+"F0.wireOp",EDGE,"E8.5")])],"isStart":true});
            var Q13;
            Q13=makeQuery(id+"F1.opExtrude","CAP_EDGE",EDGE,{"disambiguationData":[OSD([sQuery(id+"F0.wireOp",EDGE,"E80")])],"isStart":true});
            var Q14;
            Q14=makeQuery(id+"F1.opExtrude","CAP_EDGE",EDGE,{"disambiguationData":[OSD([sQuery(id+"F0.wireOp",EDGE,"E6.0")])],"isStart":true});
            var Q15;
            Q15=makeQuery(id+"F1.opExtrude","CAP_EDGE",EDGE,{"disambiguationData":[OSD([sQuery(id+"F0.wireOp",EDGE,"E6.5")])],"isStart":true});
            var Q16;
            Q16=makeQuery(id+"F1.opExtrude","CAP_EDGE",EDGE,{"disambiguationData":[OSD([sQuery(id+"F0.wireOp",EDGE,"E4.5")])],"isStart":true});
            var Q17;
            Q17=makeQuery(id+"F1.opExtrude","CAP_EDGE",EDGE,{"disambiguationData":[OSD([sQuery(id+"F0.wireOp",EDGE,"E6.4")])],"isStart":true});
            var Q18;
            Q18=makeQuery(id+"F1.opExtrude","CAP_EDGE",EDGE,{"disambiguationData":[OSD([sQuery(id+"F0.wireOp",EDGE,"E6.3")])],"isStart":true});
            var Q19;
            Q19=makeQuery(id+"F1.opExtrude","CAP_EDGE",EDGE,{"disambiguationData":[OSD([sQuery(id+"F0.wireOp",EDGE,"E4.4")])],"isStart":true});
            var Q20;
            Q20=makeQuery(id+"F1.opExtrude","CAP_EDGE",EDGE,{"disambiguationData":[OSD([sQuery(id+"F0.wireOp",EDGE,"E4.3")])],"isStart":true});
            var Q21;
            Q21=makeQuery(id+"F1.opExtrude","CAP_EDGE",EDGE,{"disambiguationData":[OSD([sQuery(id+"F0.wireOp",EDGE,"E4.2")])],"isStart":true});
            var Q22;
            Q22=makeQuery(id+"F1.opExtrude","CAP_EDGE",EDGE,{"disambiguationData":[OSD([sQuery(id+"F0.wireOp",EDGE,"E4.1")])],"isStart":true});
            var Q23;
            Q23=makeQuery(id+"F1.opExtrude","CAP_EDGE",EDGE,{"disambiguationData":[OSD([sQuery(id+"F0.wireOp",EDGE,"E4.0")])],"isStart":true});
            var Q24;
            Q24=makeQuery(id+"F1.opExtrude","CAP_EDGE",EDGE,{"disambiguationData":[OSD([sQuery(id+"F0.wireOp",EDGE,"E2.1")])],"isStart":true});
            var Q25;
            Q25=makeQuery(id+"F1.opExtrude","CAP_EDGE",EDGE,{"disambiguationData":[OSD([sQuery(id+"F0.wireOp",EDGE,"E2.0")])],"isStart":true});
            var Q26;
            Q26=makeQuery(id+"F1.opExtrude","CAP_EDGE",EDGE,{"disambiguationData":[OSD([sQuery(id+"F0.wireOp",EDGE,"E2.5")])],"isStart":true});
            var Q27;
            Q27=makeQuery(id+"F1.opExtrude","CAP_EDGE",EDGE,{"disambiguationData":[OSD([sQuery(id+"F0.wireOp",EDGE,"E2.4")])],"isStart":true});
            var Q28;
            Q28=makeQuery(id+"F1.opExtrude","CAP_EDGE",EDGE,{"disambiguationData":[OSD([sQuery(id+"F0.wireOp",EDGE,"E2.3")])],"isStart":true});
            var Q29;
            Q29=makeQuery(id+"F1.opExtrude","CAP_EDGE",EDGE,{"disambiguationData":[OSD([sQuery(id+"F0.wireOp",EDGE,"E2.2")])],"isStart":true});
            chamfer(context, id + "F8", {"entities" : qUnion([Q0, Q1, Q2, Q3, Q4, Q5, Q6, Q7, Q8, Q9, Q10, Q11, Q12, Q13, Q14, Q15, Q16, Q17, Q18, Q19, Q20, Q21, Q22, Q23, Q24, Q25, Q26, Q27, Q28, Q29]), "width" : 1 * mm, "tangentPropagation" : true});
        }
        {
            var Q0;
            {var subQ0=sQuery(id+"F0.wireOp",EDGE,"E0.5");var subQ1=sQuery(id+"F0.wireOp",EDGE,"E0.4");Q0=makeQuery(id+"F3.boolean.opBoolean","MERGE",EDGE,{"derivedFrom":[makeQuery(id+"F1.opExtrude","SWEPT_EDGE",EDGE,{"disambiguationData":[OSD([subQ1,subQ0])]}),makeQuery(id+"F3.opExtrude","SWEPT_EDGE",EDGE,{"disambiguationData":[OSD([subQ1,subQ0])]})]});}
            var Q1;
            {var subQ0=sQuery(id+"F0.wireOp",EDGE,"E0.4");var subQ1=sQuery(id+"F0.wireOp",EDGE,"E0.3");Q1=makeQuery(id+"F3.boolean.opBoolean","MERGE",EDGE,{"derivedFrom":[makeQuery(id+"F1.opExtrude","SWEPT_EDGE",EDGE,{"disambiguationData":[OSD([subQ1,subQ0])]}),makeQuery(id+"F3.opExtrude","SWEPT_EDGE",EDGE,{"disambiguationData":[OSD([subQ1,subQ0])]})]});}
            var Q2;
            {var subQ0=sQuery(id+"F0.wireOp",EDGE,"E0.3");var subQ1=sQuery(id+"F0.wireOp",EDGE,"E0.2");Q2=makeQuery(id+"F3.boolean.opBoolean","MERGE",EDGE,{"derivedFrom":[makeQuery(id+"F1.opExtrude","SWEPT_EDGE",EDGE,{"disambiguationData":[OSD([subQ1,subQ0])]}),makeQuery(id+"F3.opExtrude","SWEPT_EDGE",EDGE,{"disambiguationData":[OSD([subQ1,subQ0])]})]});}
            var Q3;
            {var subQ0=sQuery(id+"F0.wireOp",EDGE,"E0.2");var subQ1=sQuery(id+"F0.wireOp",EDGE,"E0.1");Q3=makeQuery(id+"F3.boolean.opBoolean","MERGE",EDGE,{"derivedFrom":[makeQuery(id+"F1.opExtrude","SWEPT_EDGE",EDGE,{"disambiguationData":[OSD([subQ1,subQ0])]}),makeQuery(id+"F3.opExtrude","SWEPT_EDGE",EDGE,{"disambiguationData":[OSD([subQ1,subQ0])]})]});}
            var Q4;
            {var subQ0=sQuery(id+"F0.wireOp",EDGE,"E0.1");var subQ1=sQuery(id+"F0.wireOp",EDGE,"E0.0");Q4=makeQuery(id+"F3.boolean.opBoolean","MERGE",EDGE,{"derivedFrom":[makeQuery(id+"F1.opExtrude","SWEPT_EDGE",EDGE,{"disambiguationData":[OSD([subQ1,subQ0])]}),makeQuery(id+"F3.opExtrude","SWEPT_EDGE",EDGE,{"disambiguationData":[OSD([subQ1,subQ0])]})]});}
            var Q5;
            {var subQ0=sQuery(id+"F0.wireOp",EDGE,"E0.5");var subQ1=sQuery(id+"F0.wireOp",EDGE,"E0.0");Q5=makeQuery(id+"F3.boolean.opBoolean","MERGE",EDGE,{"derivedFrom":[makeQuery(id+"F1.opExtrude","SWEPT_EDGE",EDGE,{"disambiguationData":[OSD([subQ1,subQ0])]}),makeQuery(id+"F3.opExtrude","SWEPT_EDGE",EDGE,{"disambiguationData":[OSD([subQ1,subQ0])]})]});}
            fillet(context, id + "F9", {"entities" : qUnion([Q0, Q1, Q2, Q3, Q4, Q5]), "radius" : .5 * mm, "tangentPropagation" : true, "allowEdgeOverflow" : false});
        }
    });
